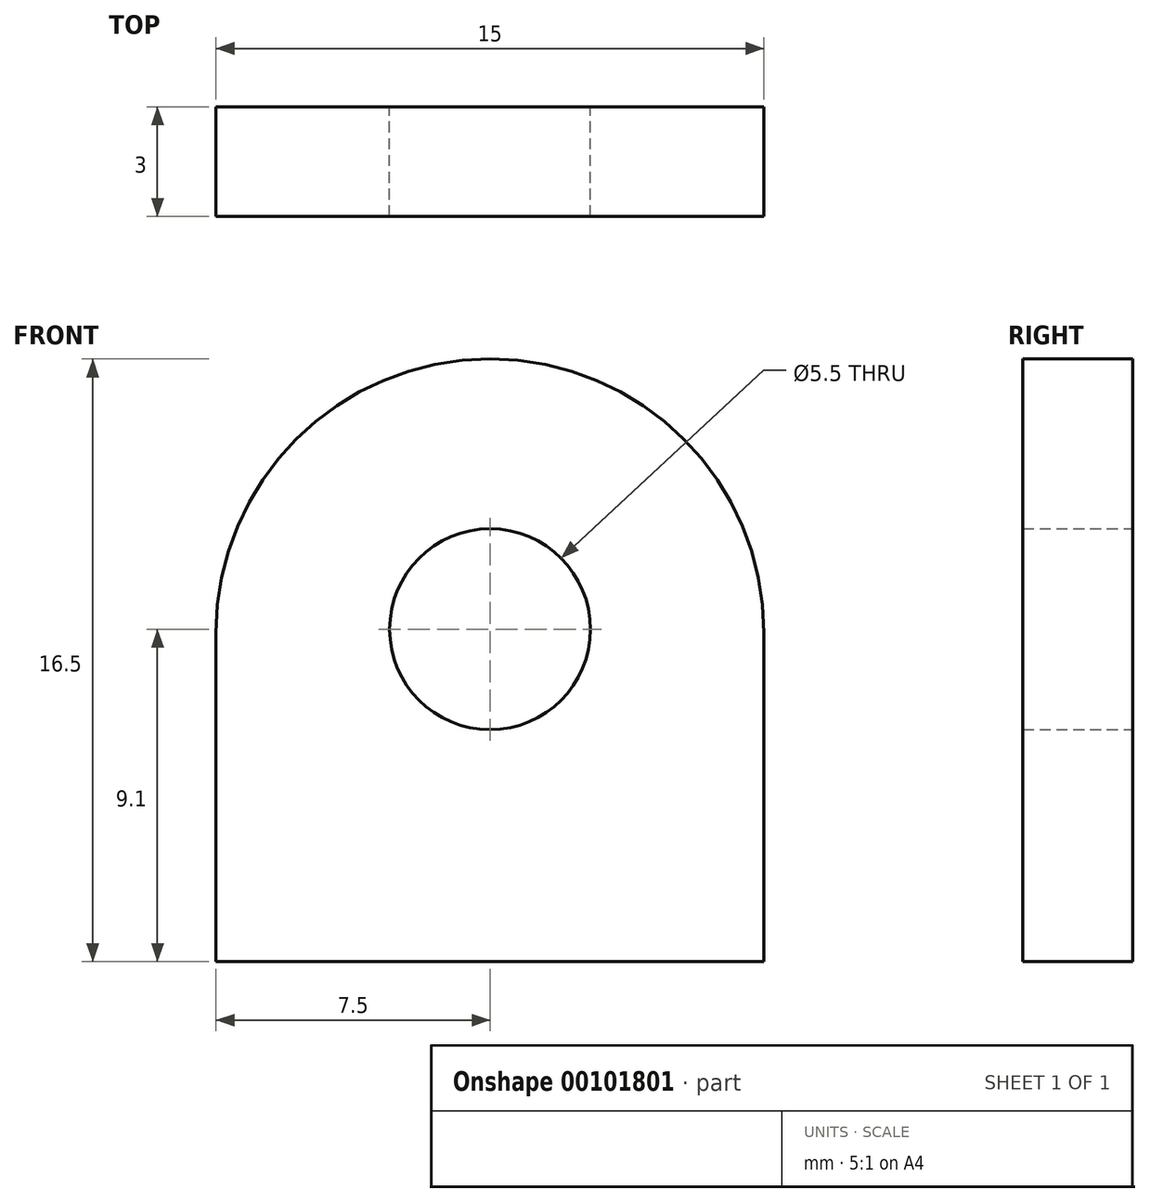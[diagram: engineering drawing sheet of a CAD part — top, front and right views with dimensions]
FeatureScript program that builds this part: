
annotation { "Feature Type Name" : "Feature", "Feature Type Description" : "" }
export const myFeature = defineFeature(function(context is Context, id is Id, definition is map)
    precondition{}
    {
        {
            var Q0;
            Q0=qCreatedBy(makeId("Top.planeOp"),FACE);
            var sketch = newSketch(context, id + "F0", { "sketchPlane" : qUnion([Q0])});
            skLineSegment(sketch, "E0.bottom", {"start": v(-7.5, -1.5) * mm, "end": v(7.5, -1.5) * mm});
            skLineSegment(sketch, "E0.top", {"start": v(-7.5, 1.5) * mm, "end": v(7.5, 1.5) * mm});
            skLineSegment(sketch, "E0.left", {"start": v(-7.5, -1.5) * mm, "end": v(-7.5, 1.5) * mm});
            skLineSegment(sketch, "E0.right", {"start": v(7.5, -1.5) * mm, "end": v(7.5, 1.5) * mm});
            skPoint(sketch, "E0.middle", {"position": v(0, 0) * mm});
            skSolve(sketch);
        }
        {
            var Q0;
            Q0 = qSketchRegion(id + "F0", true);
            extrude(context, id + "F1", {"entities" : qUnion([Q0]), "depth" : 16.5 * mm});
        }
        {
            var Q0;
            Q0=makeQuery(id+"F1.opExtrude","SWEPT_FACE",FACE,{"disambiguationData":[OSD([sQuery(id+"F0.wireOp",EDGE,"E0.top")])]});
            var sketch = newSketch(context, id + "F2", { "sketchPlane" : qUnion([Q0])});
            skCircle(sketch, "E1", {"center": v(0, 9.1) * mm, "radius": 2.75 * mm});
            skPoint(sketch, "E1.centerSnap0", {"position": v(0, 16.5) * mm});
            skSolve(sketch);
        }
        {
            var Q0;
            Q0 = qSketchRegion(id + "F2", true);
            extrude(context, id + "F3", {"entities" : qUnion([Q0]), "operationType" : NewBodyOperationType.REMOVE, "oppositeDirection" : true, "depth" : 25 * mm});
        }
        {
            var Q0;
            Q0=makeQuery(id+"F1.opExtrude","CAP_EDGE",EDGE,{"disambiguationData":[OSD([sQuery(id+"F0.wireOp",EDGE,"E0.left")])],"isStart":false});
            var Q1;
            Q1=makeQuery(id+"F1.opExtrude","CAP_EDGE",EDGE,{"disambiguationData":[OSD([sQuery(id+"F0.wireOp",EDGE,"E0.right")])],"isStart":false});
            fillet(context, id + "F4", {"entities" : qUnion([Q0, Q1]), "radius" : 7.5 * mm, "tangentPropagation" : true, "allowEdgeOverflow" : false});
        }
    });
